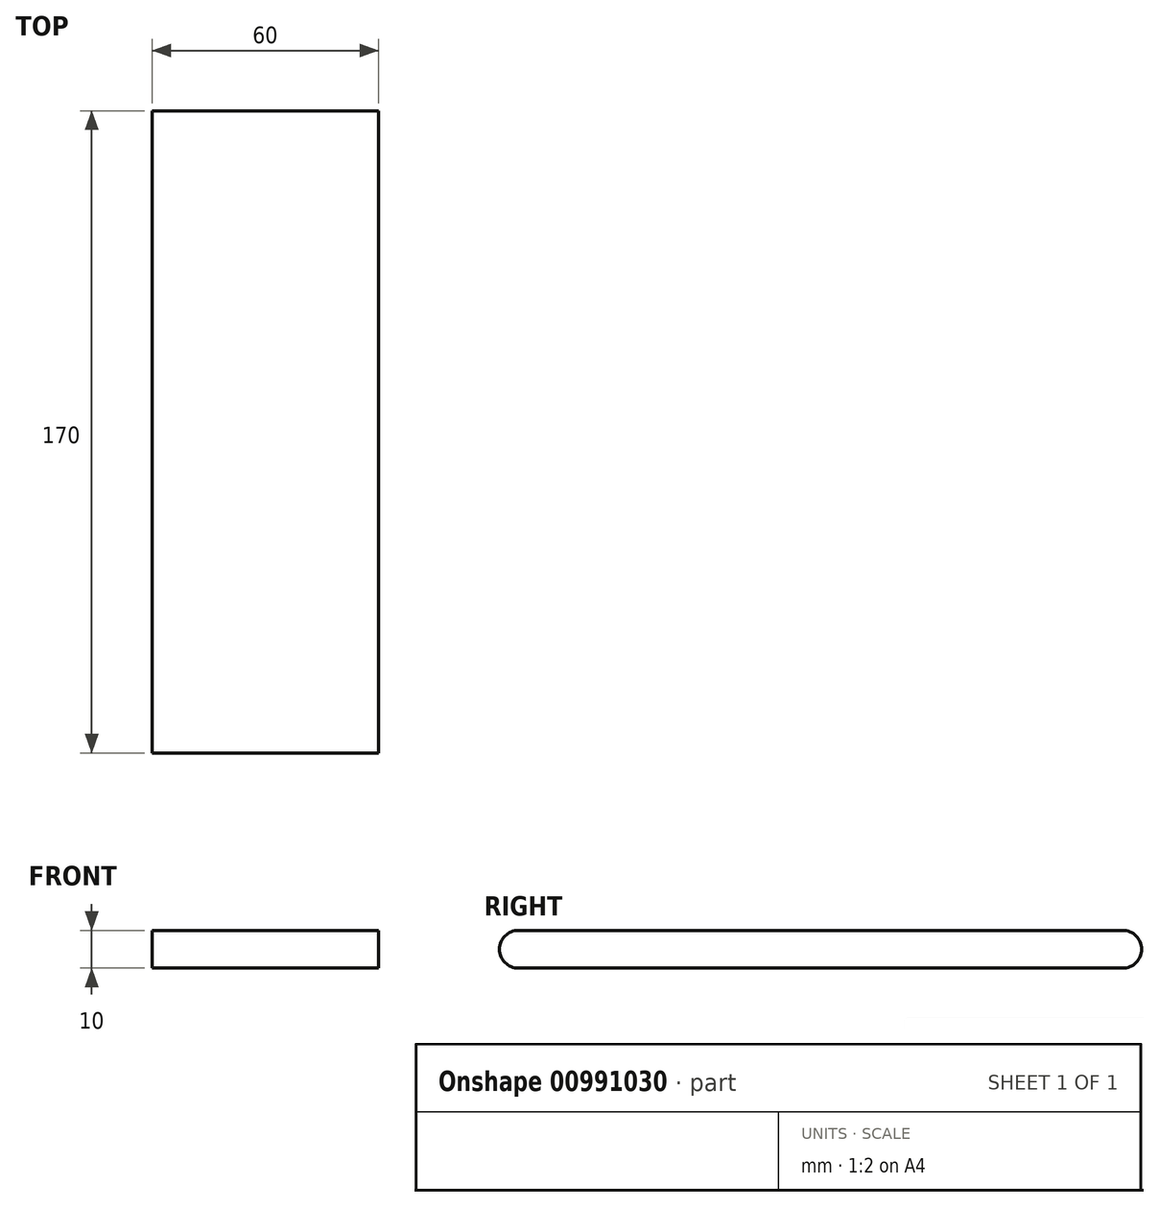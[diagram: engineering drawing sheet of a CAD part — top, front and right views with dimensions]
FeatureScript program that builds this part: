
annotation { "Feature Type Name" : "Feature", "Feature Type Description" : "" }
export const myFeature = defineFeature(function(context is Context, id is Id, definition is map)
    precondition{}
    {
        {
            var Q0;
            Q0=qCreatedBy(makeId("Right.planeOp"),FACE);
            var sketch = newSketch(context, id + "F0", { "sketchPlane" : qUnion([Q0])});
            skLineSegment(sketch, "E0.bottom", {"start": v(80, 5) * mm, "end": v(-80, 5) * mm});
            skLineSegment(sketch, "E0.top", {"start": v(80, -5) * mm, "end": v(-80, -5) * mm});
            skLineSegment(sketch, "E0.left", {"start": v(85, 0) * mm, "end": v(85, 0) * mm});
            skLineSegment(sketch, "E0.right", {"start": v(-85, 0) * mm, "end": v(-85, 0) * mm});
            skPoint(sketch, "E0.middle", {"position": v(0, 0) * mm});
            skPoint(sketch, "E1.visualSharp", {"position": v(-85, 5) * mm});
            skArc(sketch, "E1.filletArc", {"start": v(-80, 5) * mm, "mid": v(-83.54, 3.54) * mm, "end": v(-85, 0) * mm});
            skPoint(sketch, "E2.visualSharp", {"position": v(-85, -5) * mm});
            skArc(sketch, "E2.filletArc", {"start": v(-85, 0) * mm, "mid": v(-83.54, -3.54) * mm, "end": v(-80, -5) * mm});
            skPoint(sketch, "E3.visualSharp", {"position": v(85, 5) * mm});
            skArc(sketch, "E3.filletArc", {"start": v(85, 0) * mm, "mid": v(83.54, 3.54) * mm, "end": v(80, 5) * mm});
            skPoint(sketch, "E4.visualSharp", {"position": v(85, -5) * mm});
            skArc(sketch, "E4.filletArc", {"start": v(80, -5) * mm, "mid": v(83.54, -3.54) * mm, "end": v(85, 0) * mm});
            skSolve(sketch);
        }
        {
            var Q0;
            Q0 = qSketchRegion(id + "F0", true);
            extrude(context, id + "F1", {"entities" : qUnion([Q0]), "endBound" : BoundingType.SYMMETRIC, "depth" : 60 * mm, "offsetDistance" : 25 * mm});
        }
    });
